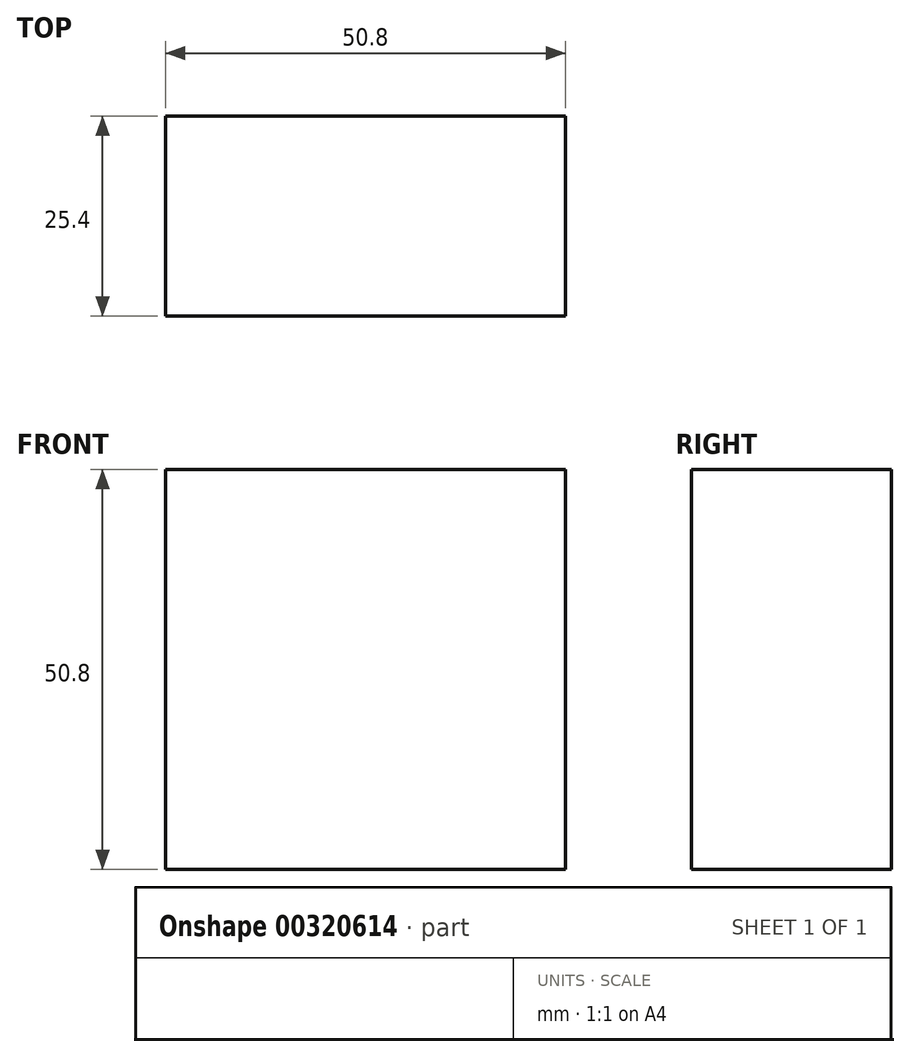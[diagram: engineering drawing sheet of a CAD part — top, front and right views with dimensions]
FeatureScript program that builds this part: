
annotation { "Feature Type Name" : "Feature", "Feature Type Description" : "" }
export const myFeature = defineFeature(function(context is Context, id is Id, definition is map)
    precondition{}
    {
        {
            var Q0;
            Q0=qCreatedBy(makeId("Front.planeOp"),FACE);
            var sketch = newSketch(context, id + "F0", { "sketchPlane" : qUnion([Q0])});
            skLineSegment(sketch, "E0.bottom", {"start": v(25.4, 25.4) * mm, "end": v(-25.4, 25.4) * mm});
            skLineSegment(sketch, "E0.top", {"start": v(25.4, -25.4) * mm, "end": v(-25.4, -25.4) * mm});
            skLineSegment(sketch, "E0.left", {"start": v(25.4, 25.4) * mm, "end": v(25.4, -25.4) * mm});
            skLineSegment(sketch, "E0.right", {"start": v(-25.4, 25.4) * mm, "end": v(-25.4, -25.4) * mm});
            skPoint(sketch, "E0.middle", {"position": v(0, 0) * mm});
            skSolve(sketch);
        }
        {
            var Q0;
            Q0=makeQuery(id+"F0.imprint","IMPRINT",FACE,{"disambiguationData":[TD([[makeQuery(id+"F0.imprint","IMPRINT",EDGE,{"derivedFrom":sQuery(id+"F0.wireOp",EDGE,"E0.bottom")}),1.0]])]});
            var sketch = newSketch(context, id + "F1", { "sketchPlane" : qUnion([Q0])});
            skLineSegment(sketch, "E1.bottom", {"start": v(25.4, 25.4) * mm, "end": v(-25.4, 25.4) * mm});
            skLineSegment(sketch, "E1.top", {"start": v(25.4, -25.4) * mm, "end": v(-25.4, -25.4) * mm});
            skLineSegment(sketch, "E1.left", {"start": v(25.4, 25.4) * mm, "end": v(25.4, -25.4) * mm});
            skLineSegment(sketch, "E1.right", {"start": v(-25.4, 25.4) * mm, "end": v(-25.4, -25.4) * mm});
            skPoint(sketch, "E1.middle", {"position": v(0, 0) * mm});
            skSolve(sketch);
        }
        {
            var Q0;
            Q0 = qSketchRegion(id + "F1", true);
            extrude(context, id + "F2", {"entities" : qUnion([Q0]), "depth" : 25.4 * mm});
        }
    });
